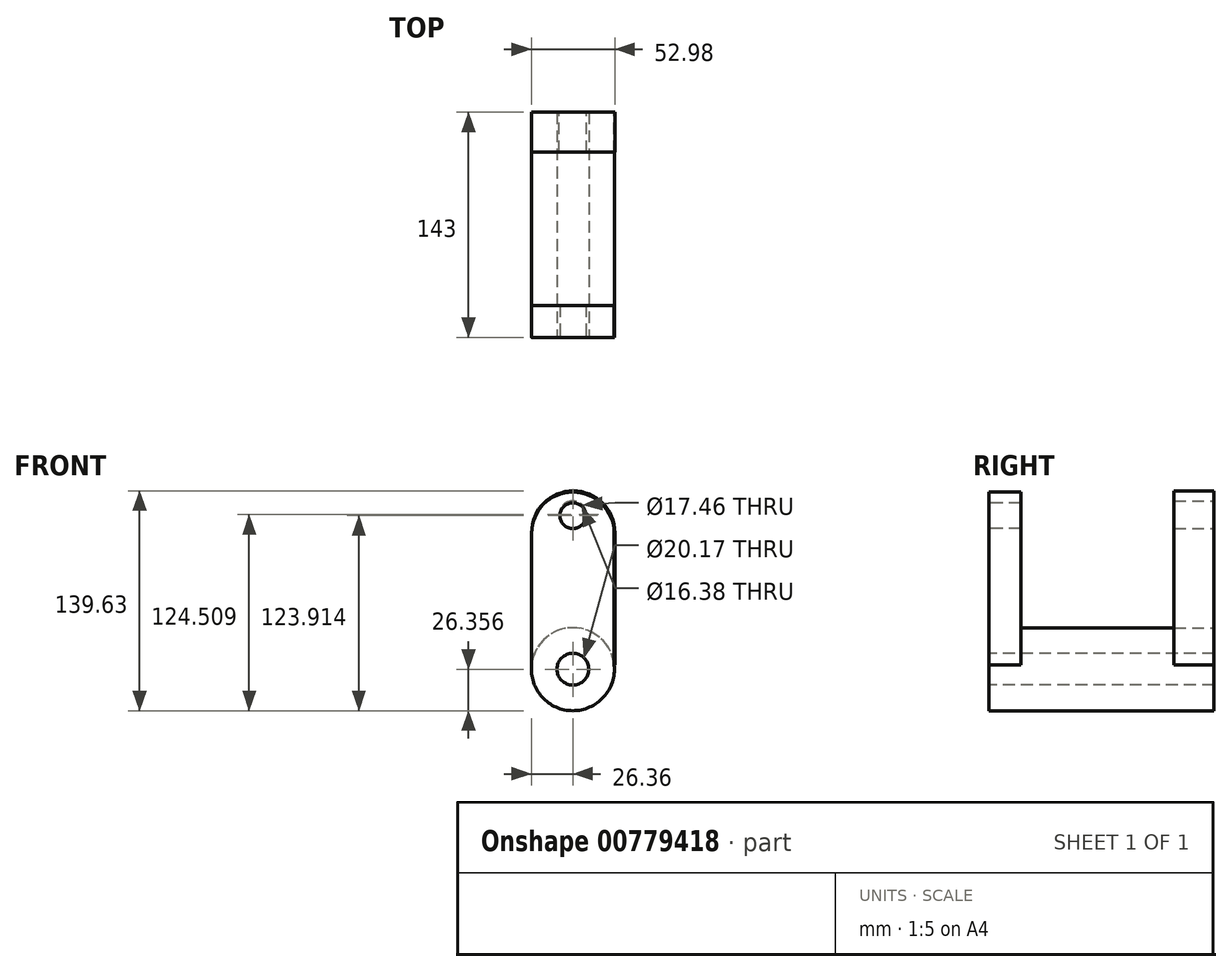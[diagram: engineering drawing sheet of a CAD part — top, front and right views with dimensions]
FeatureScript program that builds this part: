
annotation { "Feature Type Name" : "Feature", "Feature Type Description" : "" }
export const myFeature = defineFeature(function(context is Context, id is Id, definition is map)
    precondition{}
    {
        {
            var Q0;
            Q0=qCreatedBy(makeId("Front.planeOp"),FACE);
            var sketch = newSketch(context, id + "F0", { "sketchPlane" : qUnion([Q0])});
            skCircle(sketch, "E0", {"center": v(0, -43.57) * mm, "radius": 26.36 * mm});
            skArc(sketch, "E1", {"start": v(26.23, 42.68) * mm, "mid": v(0, 68.9) * mm, "end": v(-26.23, 42.68) * mm});
            skLineSegment(sketch, "E2.bottom", {"start": v(-26.23, 42.68) * mm, "end": v(26.23, 42.68) * mm});
            skLineSegment(sketch, "E2.left", {"start": v(-26.23, 42.68) * mm, "end": v(-26.23, -40.9) * mm});
            skLineSegment(sketch, "E2.right", {"start": v(26.23, 42.68) * mm, "end": v(26.23, -40.9) * mm});
            skCircle(sketch, "E3", {"center": v(0, 53.98) * mm, "radius": 8.2 * mm});
            skCircle(sketch, "E4", {"center": v(0, -43.57) * mm, "radius": 10.08 * mm});
            skSolve(sketch);
        }
        {
            var Q0;
            Q0=makeQuery(id+"F0.imprint","IMPRINT",FACE,{"disambiguationData":[TD([[makeQuery(id+"F0.imprint","IMPRINT",EDGE,{"derivedFrom":sQuery(id+"F0.wireOp",EDGE,"E4")}),-1.0]])]});
            extrude(context, id + "F1", {"entities" : qUnion([Q0]), "oppositeDirection" : true, "depth" : 143 * mm, "offsetDistance" : 25.4 * mm});
        }
        {
            var Q0;
            Q0=makeQuery(id+"F0.imprint","IMPRINT",FACE,{"disambiguationData":[TD([[makeQuery(id+"F0.imprint","IMPRINT",EDGE,{"derivedFrom":sQuery(id+"F0.wireOp",EDGE,"E2.bottom")}),-1.0]])]});
            var Q1;
            Q1=makeQuery(id+"F0.imprint","IMPRINT",FACE,{"disambiguationData":[TD([[makeQuery(id+"F0.imprint","IMPRINT",EDGE,{"derivedFrom":sQuery(id+"F0.wireOp",EDGE,"E1")}),1.0]])]});
            extrude(context, id + "F2", {"entities" : qUnion([Q0, Q1]), "operationType" : NewBodyOperationType.ADD, "oppositeDirection" : true, "depth" : 20.32 * mm, "offsetDistance" : 25.4 * mm});
        }
        {
            var Q0;
            Q0=makeQuery(id+"F1.opExtrude","CAP_FACE",FACE,{"disambiguationData":[OSD([sQuery(id+"F0.wireOp",EDGE,"E0"),sQuery(id+"F0.wireOp",EDGE,"E4")])],"isStart":false});
            var sketch = newSketch(context, id + "F3", { "sketchPlane" : qUnion([Q0])});
            skLineSegment(sketch, "E5.top", {"start": v(-26.62, -40.94) * mm, "end": v(26.23, -40.94) * mm});
            skLineSegment(sketch, "E5.left", {"start": v(-26.62, 43.28) * mm, "end": v(-26.62, -40.94) * mm});
            skLineSegment(sketch, "E5.right", {"start": v(26.23, 43.28) * mm, "end": v(26.23, -40.94) * mm});
            skArc(sketch, "E6", {"start": v(26.23, 43.28) * mm, "mid": v(-0.2, 69.7) * mm, "end": v(-26.62, 43.28) * mm});
            skCircle(sketch, "E7", {"center": v(0, 54.58) * mm, "radius": 8.73 * mm});
            skSolve(sketch);
        }
        {
            var Q0;
            {var subQ0=sQuery(id+"F3.wireOp",EDGE,"E5.left");Q0=makeQuery(id+"F3.imprint","IMPRINT",FACE,{"disambiguationData":[TD([[makeQuery(id+"F3.imprint","IMPRINT",EDGE,{"derivedFrom":subQ0}),1.0]])]});}
            extrude(context, id + "F4", {"entities" : qUnion([Q0]), "oppositeDirection" : true, "depth" : 25.4 * mm, "offsetDistance" : 25.4 * mm});
        }
    });
